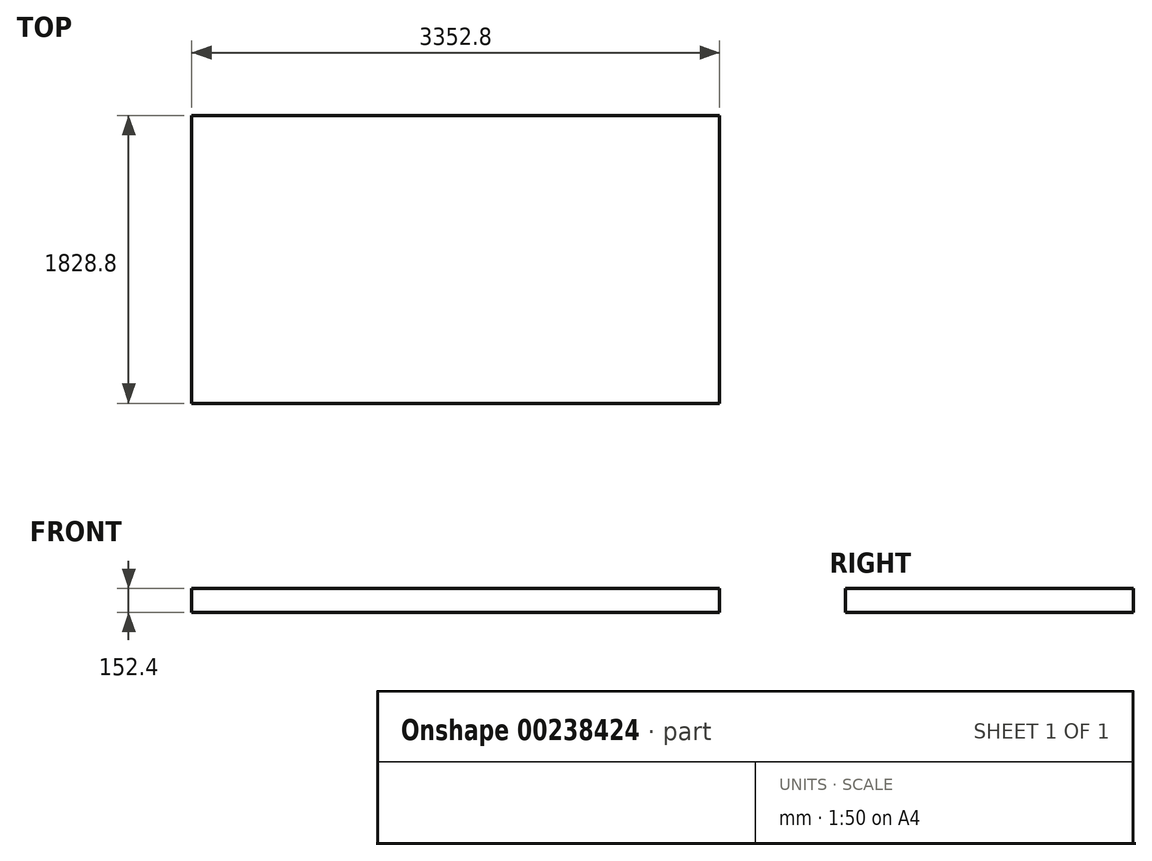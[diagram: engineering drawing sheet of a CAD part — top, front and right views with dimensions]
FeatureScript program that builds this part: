
annotation { "Feature Type Name" : "Feature", "Feature Type Description" : "" }
export const myFeature = defineFeature(function(context is Context, id is Id, definition is map)
    precondition{}
    {
        {
            var Q0;
            Q0=qCreatedBy(makeId("Top.planeOp"),FACE);
            var sketch = newSketch(context, id + "F0", { "sketchPlane" : qUnion([Q0])});
            skLineSegment(sketch, "E0.bottom", {"start": v(-1676.95, 151.72) * mm, "end": v(1675.85, 151.72) * mm});
            skLineSegment(sketch, "E0.top", {"start": v(-1676.95, -1677.08) * mm, "end": v(1675.85, -1677.08) * mm});
            skLineSegment(sketch, "E0.left", {"start": v(-1676.95, 151.72) * mm, "end": v(-1676.95, -1677.08) * mm});
            skLineSegment(sketch, "E0.right", {"start": v(1675.85, 151.72) * mm, "end": v(1675.85, -1677.08) * mm});
            skSolve(sketch);
        }
        {
            var Q0;
            Q0=makeQuery(id+"F0.imprint","IMPRINT",FACE,{"disambiguationData":[TD([[makeQuery(id+"F0.imprint","IMPRINT",EDGE,{"derivedFrom":sQuery(id+"F0.wireOp",EDGE,"E0.bottom")}),-1.0]])]});
            extrude(context, id + "F1", {"entities" : qUnion([Q0]), "depth" : 152.4 * mm});
        }
    });
